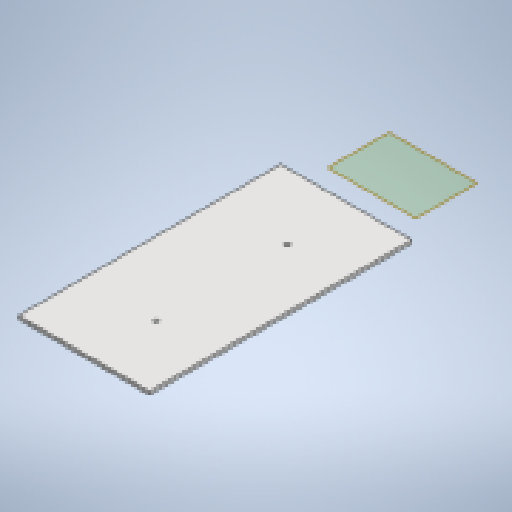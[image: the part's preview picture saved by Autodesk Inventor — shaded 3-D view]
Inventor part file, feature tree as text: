
AUTODESK INVENTOR PART (.ipt)
format: ipt  version: 2023.1 (Build 271208000, 208)  size: 136,704 bytes
history: native  units: in
note: dims shown in document units (in); Inventor stores cm internally (conversion verified against a paired STEP export)
features: other x2, plane x1, extrude x1, sketch x1
ambient origin geometry x8: Origin, YZ Plane, XZ Plane, XY Plane, X Axis, Y Axis, Z Axis, Center Point
bodies: Solid1 (feature_tree)
feature tree (5):
  plane  "Work Plane1"
  extrude  "Extrusion1"  Depth=9.8425in
  sketch  "Sketch1"  dims[d0=4.9213in d1=9.8425in d2=0.1969in d3=0.1969in d4=4.9409in d5=0.1181in d6=0.0in]
  other  "Assembly1"
  other  "knob_holder:1"
